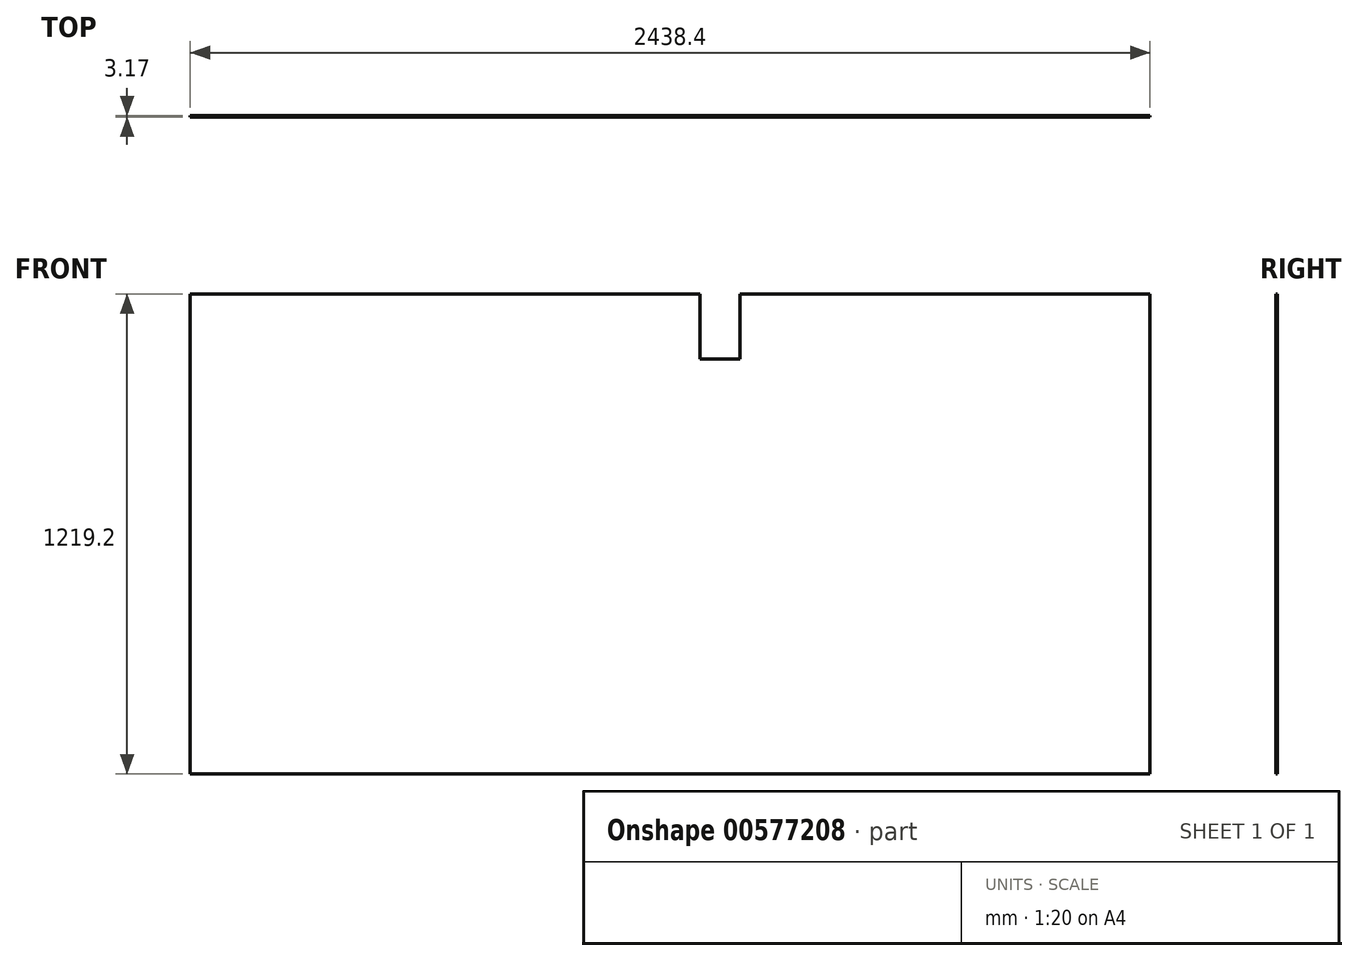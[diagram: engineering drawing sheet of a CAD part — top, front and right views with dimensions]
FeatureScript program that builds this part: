
annotation { "Feature Type Name" : "Feature", "Feature Type Description" : "" }
export const myFeature = defineFeature(function(context is Context, id is Id, definition is map)
    precondition{}
    {
        {
            var Q0;
            Q0=qCreatedBy(makeId("Front.planeOp"),FACE);
            var sketch = newSketch(context, id + "F0", { "sketchPlane" : qUnion([Q0])});
            skLineSegment(sketch, "E0.bottom", {"start": v(1219.2, 609.6) * mm, "end": v(177.8, 609.6) * mm});
            skLineSegment(sketch, "E0.top", {"start": v(1219.2, -609.6) * mm, "end": v(-1219.2, -609.6) * mm});
            skLineSegment(sketch, "E0.left", {"start": v(1219.2, 609.6) * mm, "end": v(1219.2, -609.6) * mm});
            skLineSegment(sketch, "E0.right", {"start": v(-1219.2, 609.6) * mm, "end": v(-1219.2, -609.6) * mm});
            skPoint(sketch, "E0.middle", {"position": v(0, 0) * mm});
            skLineSegment(sketch, "E1.top", {"start": v(76.2, 444.5) * mm, "end": v(177.8, 444.5) * mm});
            skLineSegment(sketch, "E1.left", {"start": v(76.2, 609.6) * mm, "end": v(76.2, 444.5) * mm});
            skLineSegment(sketch, "E1.right", {"start": v(177.8, 609.6) * mm, "end": v(177.8, 444.5) * mm});
            skLineSegment(sketch, "E2.trimOffspring", {"start": v(76.2, 609.6) * mm, "end": v(-1219.2, 609.6) * mm});
            skSolve(sketch);
        }
        {
            var Q0;
            Q0 = qSketchRegion(id + "F0", true);
            extrude(context, id + "F1", {"entities" : qUnion([Q0]), "depth" : 3.17 * mm, "offsetDistance" : 25.4 * mm});
        }
    });
